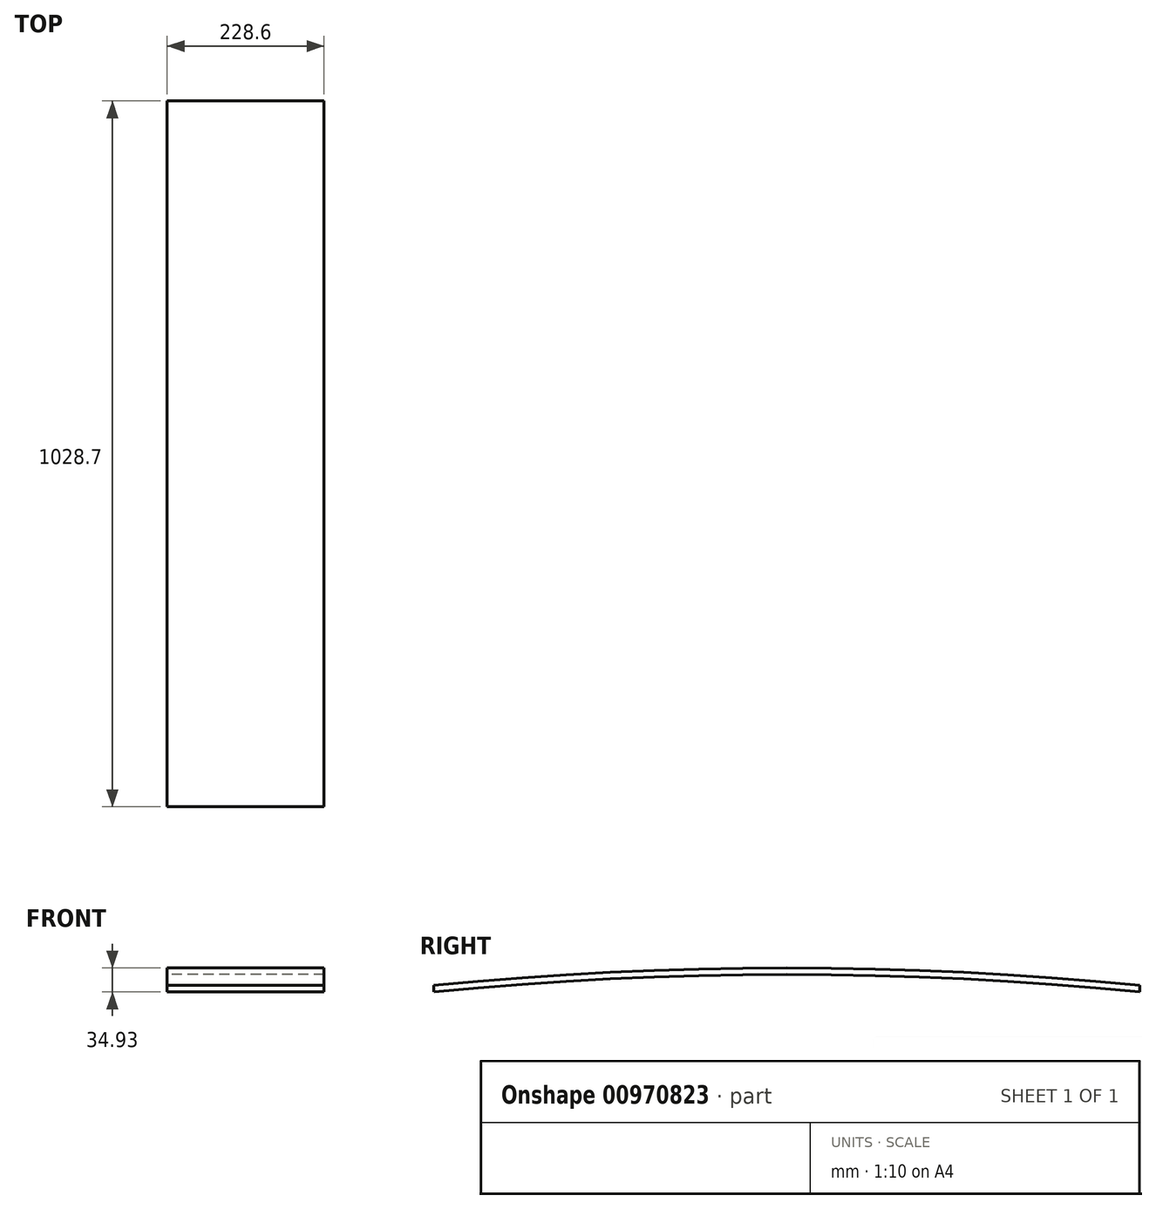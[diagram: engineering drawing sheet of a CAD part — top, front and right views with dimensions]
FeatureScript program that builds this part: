
annotation { "Feature Type Name" : "Feature", "Feature Type Description" : "" }
export const myFeature = defineFeature(function(context is Context, id is Id, definition is map)
    precondition{}
    {
        {
            var Q0;
            Q0=qCreatedBy(makeId("Right.planeOp"),FACE);
            var sketch = newSketch(context, id + "F0", { "sketchPlane" : qUnion([Q0])});
            skLineSegment(sketch, "E0", {"start": v(0, 0) * mm, "end": v(1028.7, 0) * mm, "construction": true});
            skLineSegment(sketch, "E1", {"start": v(514.35, 0) * mm, "end": v(514.35, 25.4) * mm, "construction": true});
            skArc(sketch, "E2", {"start": v(1028.7, 0) * mm, "mid": v(514.35, 25.4) * mm, "end": v(0, 0) * mm});
            skArc(sketch, "E3.0", {"start": v(1028.7, 9.57) * mm, "mid": v(514.35, 34.92) * mm, "end": v(0, 9.57) * mm});
            skLineSegment(sketch, "E4", {"start": v(0, 9.57) * mm, "end": v(0, 0) * mm});
            skLineSegment(sketch, "E5", {"start": v(1028.7, 9.57) * mm, "end": v(1028.7, 0) * mm});
            skPoint(sketch, "E6", {"position": v(101.6, 9.06) * mm});
            skPoint(sketch, "E7", {"position": v(800.1, 17.57) * mm});
            skLineSegment(sketch, "E8", {"start": v(101.6, 9.06) * mm, "end": v(197, 16.62) * mm, "construction": true});
            skLineSegment(sketch, "E9", {"start": v(800.1, 17.57) * mm, "end": v(732.3, 21.3) * mm, "construction": true});
            skLineSegment(sketch, "E10", {"start": v(800.1, 17.57) * mm, "end": v(799.14, 0) * mm, "construction": true});
            skLineSegment(sketch, "E11", {"start": v(101.6, 9.06) * mm, "end": v(102.32, 0) * mm, "construction": true});
            skSolve(sketch);
        }
        {
            var Q0;
            Q0 = qSketchRegion(id + "F0", true);
            extrude(context, id + "F1", {"entities" : qUnion([Q0]), "depth" : 114.3 * mm, "offsetDistance" : 25.4 * mm});
        }
        {
            var Q0;
            Q0=makeQuery(id+"F1.opExtrude","SWEPT_BODY",BODY,{"disambiguationData":[OSD([sQuery(id+"F0.wireOp",EDGE,"E2"),sQuery(id+"F0.wireOp",EDGE,"E3.0"),sQuery(id+"F0.wireOp",EDGE,"E4"),sQuery(id+"F0.wireOp",EDGE,"E5")])]});
            var Q1;
            Q1=makeQuery(id+"F1.opExtrude","CAP_FACE",FACE,{"disambiguationData":[OSD([sQuery(id+"F0.wireOp",EDGE,"E2"),sQuery(id+"F0.wireOp",EDGE,"E3.0"),sQuery(id+"F0.wireOp",EDGE,"E4"),sQuery(id+"F0.wireOp",EDGE,"E5")])],"isStart":true});
            mirror(context, id + "F2", {"operationType" : NewBodyOperationType.ADD, "entities" : qUnion([Q0]), "mirrorPlane" : qUnion([Q1])});
        }
    });
